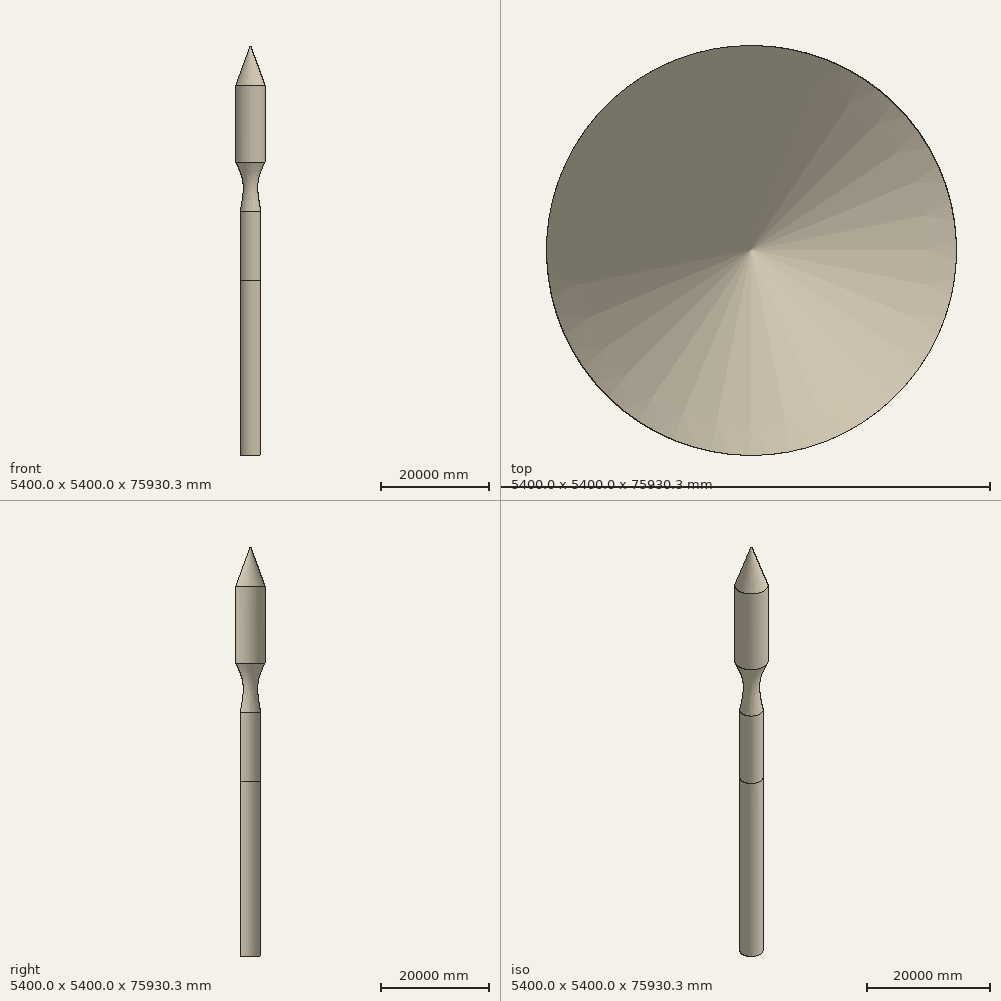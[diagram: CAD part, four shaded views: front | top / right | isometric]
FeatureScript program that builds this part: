
annotation { "Feature Type Name" : "Feature", "Feature Type Description" : "" }
export const myFeature = defineFeature(function(context is Context, id is Id, definition is map)
    precondition{}
    {
        {
            var Q0;
            Q0=qCreatedBy(makeId("Top.planeOp"),FACE);
            var sketch = newSketch(context, id + "F0", { "sketchPlane" : qUnion([Q0])});
            skCircle(sketch, "E0", {"center": v(0, 0) * mm, "radius": 1905 * mm});
            skSolve(sketch);
        }
        {
            var Q0;
            Q0=makeQuery(id+"F0.imprint","IMPRINT",FACE,{"disambiguationData":[TD([[makeQuery(id+"F0.imprint","IMPRINT",EDGE,{"derivedFrom":sQuery(id+"F0.wireOp",EDGE,"E0")}),1.0]])]});
            cPlane(context, id + "F1", {"entities" : qUnion([Q0]), "cplaneType" : CPlaneType.OFFSET, "offset" : 32491.68 * mm, "width" : 152.4 * mm, "height" : 152.4 * mm});
        }
        {
            var Q0;
            Q0=qCreatedBy(id+"F1.planeOp",FACE);
            var sketch = newSketch(context, id + "F2", { "sketchPlane" : qUnion([Q0])});
            skCircle(sketch, "E1", {"center": v(0, 0) * mm, "radius": 1915 * mm});
            skSolve(sketch);
        }
        {
            var Q0;
            Q0=makeQuery(id+"F2.imprint","IMPRINT",FACE,{"disambiguationData":[TD([[makeQuery(id+"F2.imprint","IMPRINT",EDGE,{"derivedFrom":sQuery(id+"F2.wireOp",EDGE,"E1")}),1.0]])]});
            cPlane(context, id + "F3", {"entities" : qUnion([Q0]), "cplaneType" : CPlaneType.OFFSET, "offset" : 12680 * mm, "width" : 152.4 * mm, "height" : 152.4 * mm});
        }
        {
            var Q0;
            Q0=qCreatedBy(id+"F3.planeOp",FACE);
            var sketch = newSketch(context, id + "F4", { "sketchPlane" : qUnion([Q0])});
            skCircle(sketch, "E2", {"center": v(0, 0) * mm, "radius": 1915 * mm});
            skSolve(sketch);
        }
        {
            var Q0;
            Q0=makeQuery(id+"F0.imprint","IMPRINT",FACE,{"disambiguationData":[TD([[makeQuery(id+"F0.imprint","IMPRINT",EDGE,{"derivedFrom":sQuery(id+"F0.wireOp",EDGE,"E0")}),1.0]])]});
            var Q1;
            Q1=makeQuery(id+"F2.imprint","IMPRINT",FACE,{"disambiguationData":[TD([[makeQuery(id+"F2.imprint","IMPRINT",EDGE,{"derivedFrom":sQuery(id+"F2.wireOp",EDGE,"E1")}),1.0]])]});
            loft(context, id + "F5", {"sheetProfilesArray" : [{ "sheetProfileEntities" : qUnion([Q0]) }, { "sheetProfileEntities" : qUnion([Q1]) }]});
        }
        {
            var Q1;
            Q1=makeQuery(id+"F5.opLoft","CAP_FACE",FACE,{"disambiguationData":[OSD([makeQuery(id+"F2.imprint","IMPRINT",FACE,{"disambiguationData":[TD([[makeQuery(id+"F2.imprint","IMPRINT",EDGE,{"derivedFrom":sQuery(id+"F2.wireOp",EDGE,"E1")}),1.0]])]})])],"isStart":true});
            var Q2;
            Q2=makeQuery(id+"F4.imprint","IMPRINT",FACE,{"disambiguationData":[TD([[makeQuery(id+"F4.imprint","IMPRINT",EDGE,{"derivedFrom":sQuery(id+"F4.wireOp",EDGE,"E2")}),1.0]])]});
            loft(context, id + "F6", {"sheetProfilesArray" : [{ "sheetProfileEntities" : qUnion([Q1]) }, { "sheetProfileEntities" : qUnion([Q2]) }]});
        }
        {
            var Q0;
            Q0=qCreatedBy(id+"F3.planeOp",FACE);
            cPlane(context, id + "F7", {"entities" : qUnion([Q0]), "cplaneType" : CPlaneType.OFFSET, "offset" : 23400 * mm, "width" : 152.4 * mm, "height" : 152.4 * mm});
        }
        {
            var Q0;
            Q0=qCreatedBy(id+"F7.planeOp",FACE);
            var sketch = newSketch(context, id + "F8", { "sketchPlane" : qUnion([Q0])});
            skCircle(sketch, "E3", {"center": v(0, 0) * mm, "radius": 2700 * mm});
            skSolve(sketch);
        }
        {
            var Q0;
            Q0=makeQuery(id+"F6.opLoft","CAP_FACE",FACE,{"disambiguationData":[OSD([makeQuery(id+"F4.imprint","IMPRINT",FACE,{"disambiguationData":[TD([[makeQuery(id+"F4.imprint","IMPRINT",EDGE,{"derivedFrom":sQuery(id+"F4.wireOp",EDGE,"E2")}),1.0]])]})])],"isStart":true});
            cPlane(context, id + "F9", {"entities" : qUnion([Q0]), "cplaneType" : CPlaneType.OFFSET, "offset" : 6096 * mm, "width" : 152.4 * mm, "height" : 152.4 * mm});
        }
        {
            var Q0;
            Q0=qCreatedBy(id+"F9.planeOp",FACE);
            var sketch = newSketch(context, id + "F10", { "sketchPlane" : qUnion([Q0])});
            skCircle(sketch, "E4", {"center": v(0, 0) * mm, "radius": 1525 * mm});
            skSolve(sketch);
        }
        {
            var Q0;
            Q0=qCreatedBy(id+"F9.planeOp",FACE);
            cPlane(context, id + "F11", {"entities" : qUnion([Q0]), "cplaneType" : CPlaneType.OFFSET, "offset" : 3048 * mm, "width" : 152.4 * mm, "height" : 152.4 * mm});
        }
        {
            var Q0;
            Q0=qCreatedBy(id+"F11.planeOp",FACE);
            var sketch = newSketch(context, id + "F12", { "sketchPlane" : qUnion([Q0])});
            skCircle(sketch, "E5", {"center": v(0, 0) * mm, "radius": 2700 * mm});
            skSolve(sketch);
        }
        {
            var Q0;
            Q0=makeQuery(id+"F6.opLoft","CAP_FACE",FACE,{"disambiguationData":[OSD([makeQuery(id+"F4.imprint","IMPRINT",FACE,{"disambiguationData":[TD([[makeQuery(id+"F4.imprint","IMPRINT",EDGE,{"derivedFrom":sQuery(id+"F4.wireOp",EDGE,"E2")}),1.0]])]})])],"isStart":true});
            var Q1;
            Q1=makeQuery(id+"F10.imprint","IMPRINT",FACE,{"disambiguationData":[TD([[makeQuery(id+"F10.imprint","IMPRINT",EDGE,{"derivedFrom":sQuery(id+"F10.wireOp",EDGE,"E4")}),1.0]])]});
            var Q2;
            Q2=makeQuery(id+"F12.imprint","IMPRINT",FACE,{"disambiguationData":[TD([[makeQuery(id+"F12.imprint","IMPRINT",EDGE,{"derivedFrom":sQuery(id+"F12.wireOp",EDGE,"E5")}),1.0]])]});
            loft(context, id + "F13", {"sheetProfilesArray" : [{ "sheetProfileEntities" : qUnion([Q0]) }, { "sheetProfileEntities" : qUnion([Q1]) }, { "sheetProfileEntities" : qUnion([Q2]) }]});
        }
        {
            var Q1;
            Q1=makeQuery(id+"F13.opLoft","CAP_FACE",FACE,{"disambiguationData":[OSD([makeQuery(id+"F12.imprint","IMPRINT",FACE,{"disambiguationData":[TD([[makeQuery(id+"F12.imprint","IMPRINT",EDGE,{"derivedFrom":sQuery(id+"F12.wireOp",EDGE,"E5")}),1.0]])]})])],"isStart":true});
            var Q2;
            Q2=makeQuery(id+"F8.imprint","IMPRINT",FACE,{"disambiguationData":[TD([[makeQuery(id+"F8.imprint","IMPRINT",EDGE,{"derivedFrom":sQuery(id+"F8.wireOp",EDGE,"E3")}),1.0]])]});
            loft(context, id + "F14", {"operationType" : NewBodyOperationType.ADD, "sheetProfilesArray" : [{ "sheetProfileEntities" : qUnion([Q1]) }, { "sheetProfileEntities" : qUnion([Q2]) }]});
        }
        {
            var Q0;
            Q0=makeQuery(id+"F14.opLoft","CAP_FACE",FACE,{"disambiguationData":[OSD([makeQuery(id+"F8.imprint","IMPRINT",FACE,{"disambiguationData":[TD([[makeQuery(id+"F8.imprint","IMPRINT",EDGE,{"derivedFrom":sQuery(id+"F8.wireOp",EDGE,"E3")}),1.0]])]})])],"isStart":true});
            var sketch = newSketch(context, id + "F15", { "sketchPlane" : qUnion([Q0])});
            skLineSegment(sketch, "E6", {"start": v(2700, 0) * mm, "end": v(-2700, 0) * mm});
            skSolve(sketch);
        }
        {
            var Q0;
            Q0=sQuery(id+"F15.wireOp",EDGE,"E6");
            cPlane(context, id + "F16", {"entities" : qUnion([Q0]), "cplaneType" : CPlaneType.LINE_ANGLE, "offset" : 25.4 * mm, "angle" : 180 * degree, "width" : 152.4 * mm, "height" : 152.4 * mm});
        }
        {
            var Q0;
            Q0=qCreatedBy(id+"F16.planeOp",FACE);
            var sketch = newSketch(context, id + "F17", { "sketchPlane" : qUnion([Q0])});
            skLineSegment(sketch, "E7", {"start": v(0, 68569.98) * mm, "end": v(0, 68571.68) * mm, "construction": true});
            skLineSegment(sketch, "E8", {"start": v(0, 68571.68) * mm, "end": v(2700, 68571.68) * mm});
            skLineSegment(sketch, "E9", {"start": v(2700, 68571.68) * mm, "end": v(0, 68569.98) * mm});
            skLineSegment(sketch, "E10", {"start": v(0, 68569.98) * mm, "end": v(0, 71734.69) * mm});
            skLineSegment(sketch, "E11", {"start": v(2700, 68571.68) * mm, "end": v(0, 75930.3) * mm});
            skLineSegment(sketch, "E12", {"start": v(0, 75930.3) * mm, "end": v(0, 71734.69) * mm});
            skSolve(sketch);
        }
        {
            var Q0;
            {var subQ0=sQuery(id+"F17.wireOp",EDGE,"E8");Q0=makeQuery(id+"F17.imprint","IMPRINT",FACE,{"disambiguationData":[TD([[makeQuery(id+"F17.imprint","IMPRINT",EDGE,{"derivedFrom":subQ0}),1.0]])]});}
            var Q1;
            Q1=sQuery(id+"F17.wireOp",EDGE,"E12");
            revolve(context, id + "F18", {"operationType" : NewBodyOperationType.ADD, "surfaceOperationType" : NewSurfaceOperationType.NEW, "entities" : qUnion([Q0]), "axis" : qUnion([Q1]), "revolveType" : RevolveType.FULL});
        }
    });
